# Revit family: All-Lite_EFD-437-FL_R17
name_source: partatom
category: Mechanical Equipment
units: mm (PartAtom-declared; Revit-internal decimal feet)

## family parameters
Cut with Voids When Loaded = No
Host = Face
Part Type = Normal
Room Calculation Point = No
Round Connector Dimension = Use Diameter
Shared = No

## types (2) — shared parameters
Air Volume Delivered = 9105 cfm
Assembly Code = B3020300
Blades = 37° x 0.081'' thick J- style.
Default Elevation = 0"
Depth = 4"
Description = The EFD-437-FL louver is designed to prevent water penetration
in non-wind-driven rain applications by collecting water in frame
and blade gutters and channeling it into downspouts and away
from airflow paths. The design is engineered and tested to
withstand extreme loads, debris impact, and cyclic fatigue
associated with the severe weather effects of hurricanes (Florida
Building Code approval No. FL32498). The EFD-437-FL is AMCA
540 listed, making it ideally suited for use in hurricane-prone and
windborne debris regions as per the International Building Code.
In addition, the EFD-437-FL is a UL Classified Windstorm Rated
Assembly with design pressures up to 250 psf (depending on
section size).
Design Load = Up to 250 psf
Florida Building Code Approval (2020-FBC) = No. FL32509
Frame = 4'' deep x 0.081'' thick channel.
Free Area Velocity = 1029 fpm
Manufacturer = All-Lite
Material = Mill finish 6063 extruded aluminum.
Maximum Size = 60'' x 120''
Minimum Size = 12'' x 12'
Model = EFD-437-FL
Modeled By = Commense Studio
Mullion = Visible
Pressure Loss = .16 in. wg
Screen = 1/2'' x 0.063'' expanded and flattened aluminum.
Velocity @ 0.15 in. wg. Pressure Loss = 1020 fpm

## per-type parameters (varying)
| type | Array Control 1 | Array Control 2 | Blade Width | Height | Height Control | Product URL | URL | Width | Width Control |
| 60" x 120" | 32 | 32 | 58" | 120" | 120" |  | https://www.pottorff.com | 60" | 60" |
| 36" x 48" | 11 | 11 | 34" | 48" | 48" | https://www.alllite.com | https://www.alllite.com | 36" | 36" |

## geometry (parser evidence)
native form markers: Blend x4, Sweep x6
no freeform markers — native parametric forms only
